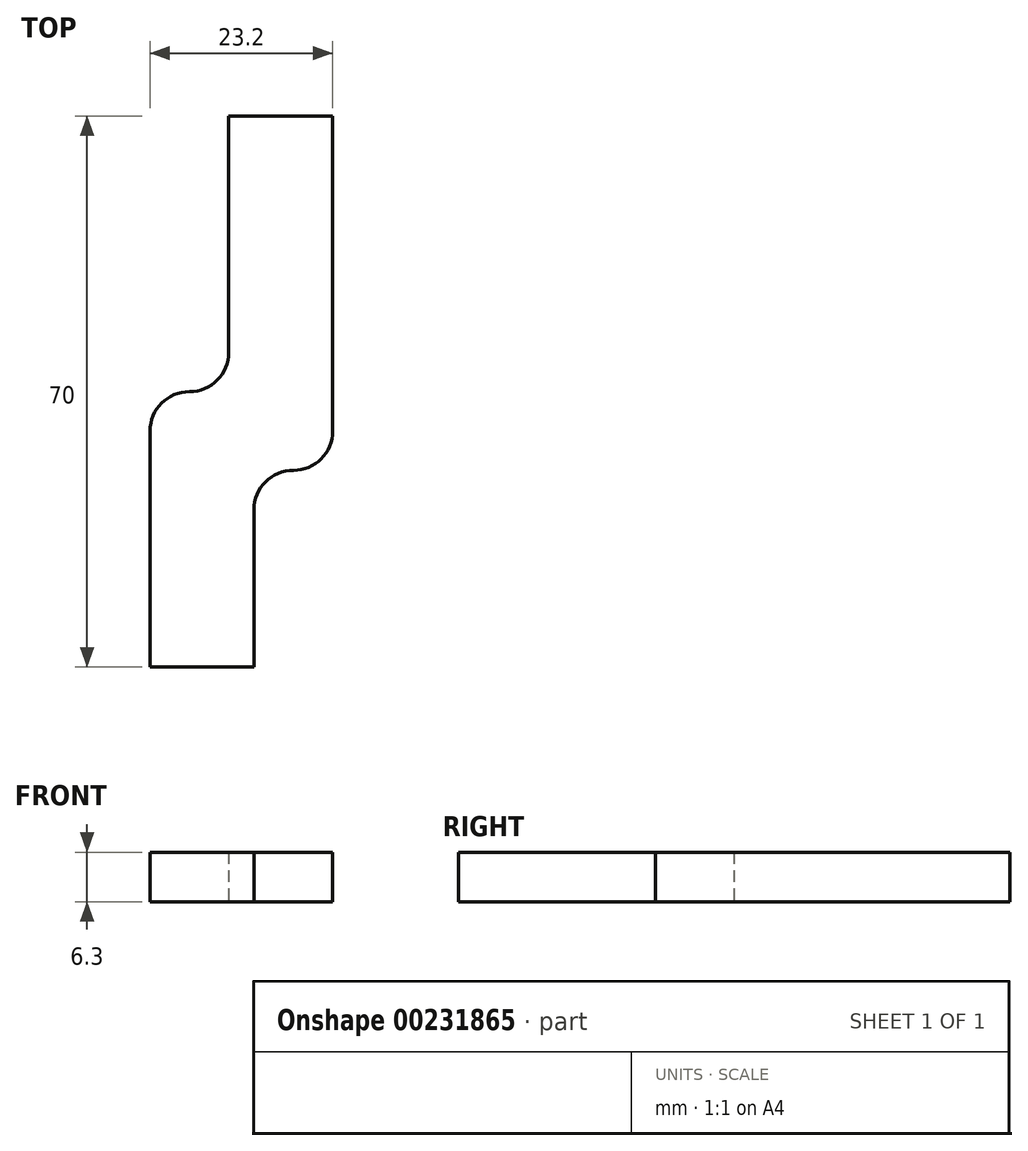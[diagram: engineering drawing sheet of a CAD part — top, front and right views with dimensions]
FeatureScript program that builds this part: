
annotation { "Feature Type Name" : "Feature", "Feature Type Description" : "" }
export const myFeature = defineFeature(function(context is Context, id is Id, definition is map)
    precondition{}
    {
        {
            var Q0;
            Q0=qCreatedBy(makeId("Top.planeOp"),FACE);
            var sketch = newSketch(context, id + "F0", { "sketchPlane" : qUnion([Q0])});
            skLineSegment(sketch, "E0", {"start": v(0, 0) * mm, "end": v(0, 30) * mm});
            skLineSegment(sketch, "E1", {"start": v(10, 70) * mm, "end": v(10, 40) * mm});
            skLineSegment(sketch, "E2", {"start": v(13.2, 0) * mm, "end": v(0, 0) * mm});
            skLineSegment(sketch, "E3", {"start": v(10, 70) * mm, "end": v(23.2, 70) * mm});
            skLineSegment(sketch, "E4", {"start": v(23.2, 70) * mm, "end": v(23.2, 30) * mm});
            skPoint(sketch, "E5.visualSharp", {"position": v(0, 30) * mm});
            skArc(sketch, "E5.filletArc", {"start": v(5, 35) * mm, "mid": v(1.46, 33.54) * mm, "end": v(0, 30) * mm});
            skArc(sketch, "E6.filletArc", {"start": v(5, 35) * mm, "mid": v(8.54, 36.46) * mm, "end": v(10, 40) * mm});
            skArc(sketch, "E7.filletArc", {"start": v(18.2, 25) * mm, "mid": v(21.74, 26.46) * mm, "end": v(23.2, 30) * mm});
            skArc(sketch, "E8.filletArc", {"start": v(18.2, 25) * mm, "mid": v(14.66, 23.54) * mm, "end": v(13.2, 20) * mm});
            skLineSegment(sketch, "E9", {"start": v(5, 35) * mm, "end": v(5, 35) * mm});
            skLineSegment(sketch, "E10", {"start": v(13.2, 0) * mm, "end": v(13.2, 20) * mm});
            skSolve(sketch);
        }
        {
            var Q0;
            Q0=makeQuery(id+"F0.imprint","IMPRINT",FACE,{"disambiguationData":[TD([[makeQuery(id+"F0.imprint","IMPRINT",EDGE,{"derivedFrom":sQuery(id+"F0.wireOp",EDGE,"E0")}),-1.0]])]});
            extrude(context, id + "F1", {"entities" : qUnion([Q0]), "depth" : 6.3 * mm});
        }
    });
